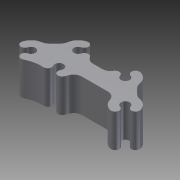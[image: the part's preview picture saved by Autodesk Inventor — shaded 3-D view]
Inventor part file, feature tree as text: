
AUTODESK INVENTOR PART (.ipt)
format: ipt  version: 2011 (Build 150239000, 239)  size: 131,072 bytes
history: native  units: mm
features: imported_body x1, plane x1
ambient origin geometry x8: Origin, YZ Plane, XZ Plane, XY Plane, X Axis, Y Axis, Z Axis, Center Point
bodies: Solid1 (feature_tree)
feature tree (2):
  imported_body  "Base1"
  plane  "Work Plane1"
